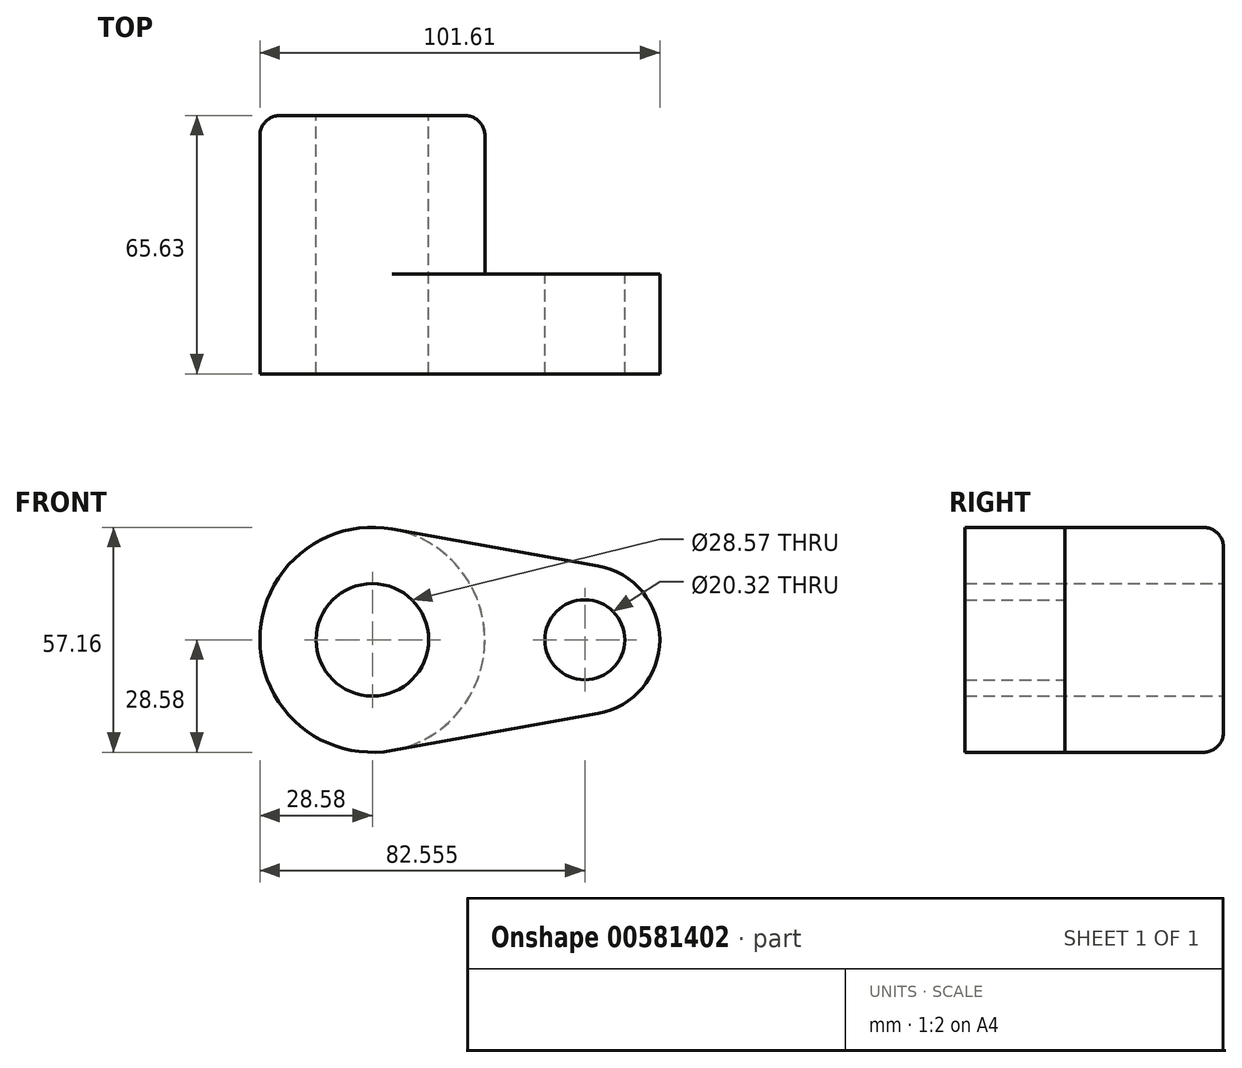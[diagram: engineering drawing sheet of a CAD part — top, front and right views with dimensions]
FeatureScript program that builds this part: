
annotation { "Feature Type Name" : "Feature", "Feature Type Description" : "" }
export const myFeature = defineFeature(function(context is Context, id is Id, definition is map)
    precondition{}
    {
        {
            var Q0;
            Q0=qCreatedBy(makeId("Front.planeOp"),FACE);
            var sketch = newSketch(context, id + "F0", { "sketchPlane" : qUnion([Q0])});
            skCircle(sketch, "E0", {"center": v(0, 0) * mm, "radius": 14.29 * mm});
            skCircle(sketch, "E1", {"center": v(0, 0) * mm, "radius": 28.58 * mm});
            skCircle(sketch, "E2", {"center": v(53.98, 0) * mm, "radius": 10.16 * mm});
            skCircle(sketch, "E3", {"center": v(53.98, 0) * mm, "radius": 19.05 * mm});
            skLineSegment(sketch, "E4", {"start": v(5.04, 28.13) * mm, "end": v(57.34, 18.75) * mm});
            skLineSegment(sketch, "E5", {"start": v(57.34, -18.75) * mm, "end": v(5.04, -28.13) * mm});
            skSolve(sketch);
        }
        {
            var Q0;
            Q0 = qSketchRegion(id + "F0", true);
            extrude(context, id + "F1", {"entities" : qUnion([Q0]), "depth" : 25.4 * mm, "offsetDistance" : 25.4 * mm});
        }
        {
            var Q0;
            Q0=makeQuery(id+"F0.imprint","IMPRINT",FACE,{"disambiguationData":[TD([[makeQuery(id+"F0.imprint","IMPRINT",EDGE,{"derivedFrom":sQuery(id+"F0.wireOp",EDGE,"E0")}),-1.0]])]});
            extrude(context, id + "F2", {"entities" : qUnion([Q0]), "operationType" : NewBodyOperationType.ADD, "oppositeDirection" : true, "depth" : 40.23 * mm, "offsetDistance" : 25.4 * mm});
        }
        {
            var Q0;
            Q0=makeQuery(id+"F2.opExtrude","CAP_EDGE",EDGE,{"disambiguationData":[OSD([sQuery(id+"F0.wireOp",EDGE,"E1")])],"isStart":false});
            fillet(context, id + "F3", {"entities" : qUnion([Q0]), "radius" : 5.08 * mm, "tangentPropagation" : true, "allowEdgeOverflow" : false});
        }
    });
